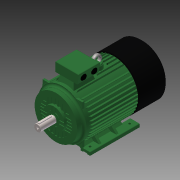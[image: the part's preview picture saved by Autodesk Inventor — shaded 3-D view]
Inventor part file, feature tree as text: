
AUTODESK INVENTOR PART (.ipt)
format: ipt  version: 2015 SP1 (Build 190203100, 203)  size: 1,019,392 bytes
history: native  units: in
note: dims shown in document units (in); Inventor stores cm internally (conversion verified against a paired STEP export)
features: other x3, imported_body x3, fillet x1
ambient origin geometry x8: Origin, YZ Plane, XZ Plane, XY Plane, X Axis, Y Axis, Z Axis, Center Point
bodies: Body1 (feature_tree), Body2 (feature_tree), Body3 (feature_tree)
feature tree (7):
  other  "Cut-Extrude3[1]"
  other  "TMDF 180L1"
  other  "Cut-Extrude3[2]"
  fillet  "Fillet3"  [1 undecoded]
  imported_body  "Base1"
  imported_body  "Base2"
  imported_body  "Base3"
note: 1 required parameter value undecoded (feature->parameter linkage not recoverable at this tier; creation-order binding heuristic only, values carry confidence <= 0.55)
